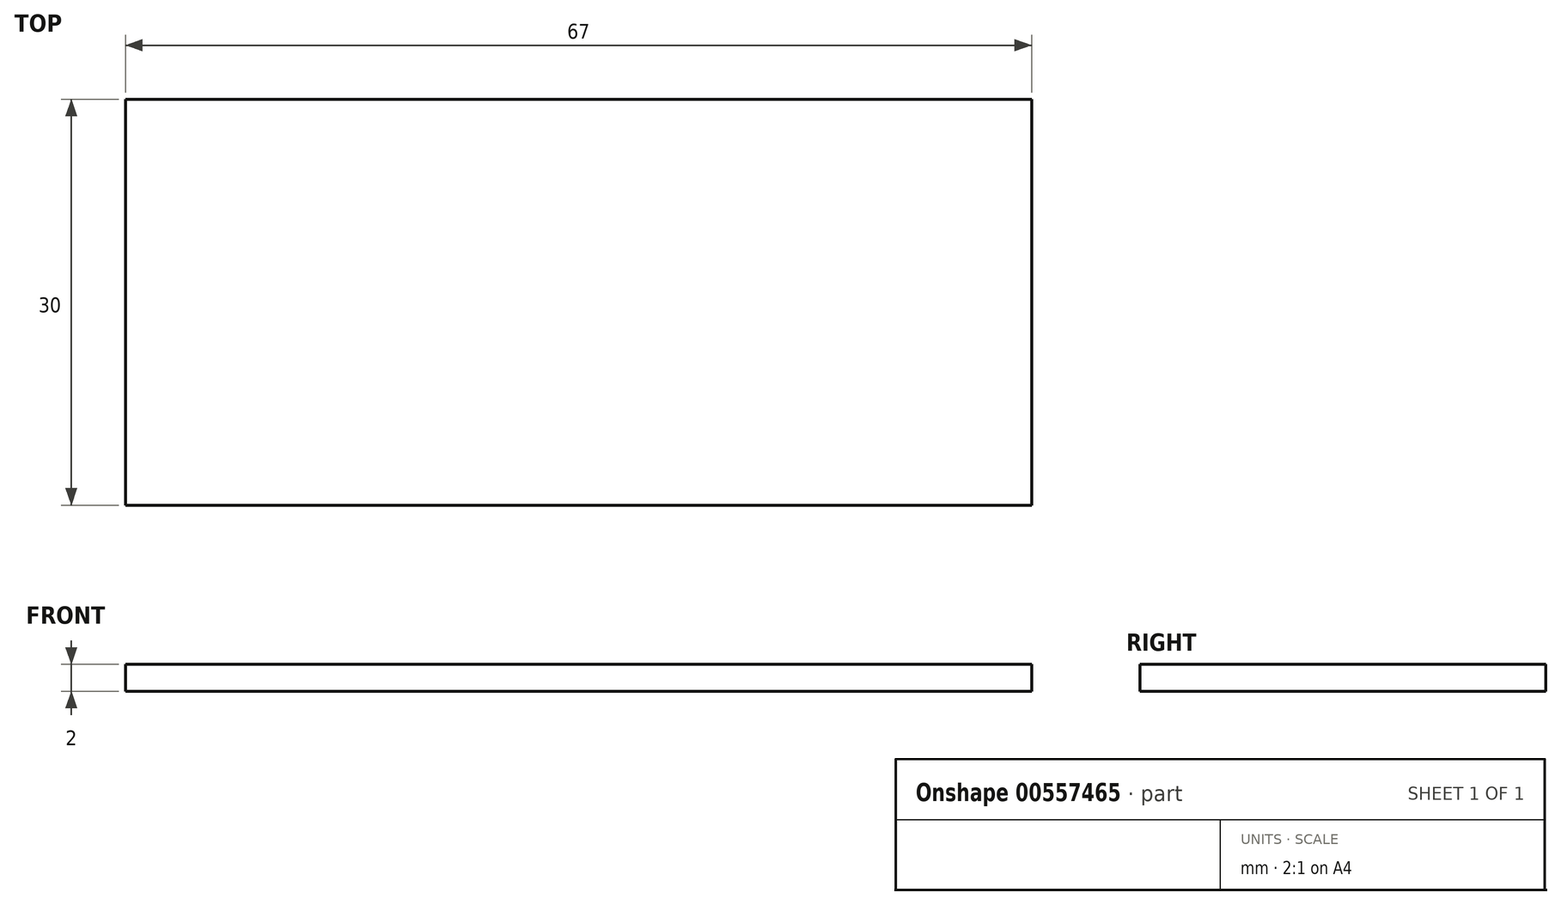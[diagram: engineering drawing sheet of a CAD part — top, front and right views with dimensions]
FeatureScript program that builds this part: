
annotation { "Feature Type Name" : "Feature", "Feature Type Description" : "" }
export const myFeature = defineFeature(function(context is Context, id is Id, definition is map)
    precondition{}
    {
        {
            var Q0;
            Q0=qCreatedBy(makeId("Top.planeOp"),FACE);
            var sketch = newSketch(context, id + "F0", { "sketchPlane" : qUnion([Q0])});
            skLineSegment(sketch, "E0.bottom", {"start": v(33.5, -15) * mm, "end": v(-33.5, -15) * mm});
            skLineSegment(sketch, "E0.top", {"start": v(33.5, 15) * mm, "end": v(-33.5, 15) * mm});
            skLineSegment(sketch, "E0.left", {"start": v(33.5, -15) * mm, "end": v(33.5, 15) * mm});
            skLineSegment(sketch, "E0.right", {"start": v(-33.5, -15) * mm, "end": v(-33.5, 15) * mm});
            skPoint(sketch, "E0.middle", {"position": v(0, 0) * mm});
            skSolve(sketch);
        }
        {
            var Q0;
            Q0=makeQuery(id+"F0.imprint","IMPRINT",FACE,{"disambiguationData":[TD([[makeQuery(id+"F0.imprint","IMPRINT",EDGE,{"derivedFrom":sQuery(id+"F0.wireOp",EDGE,"E0.bottom")}),-1.0]])]});
            extrude(context, id + "F1", {"entities" : qUnion([Q0]), "depth" : 2 * mm, "offsetDistance" : 25 * mm});
        }
    });
